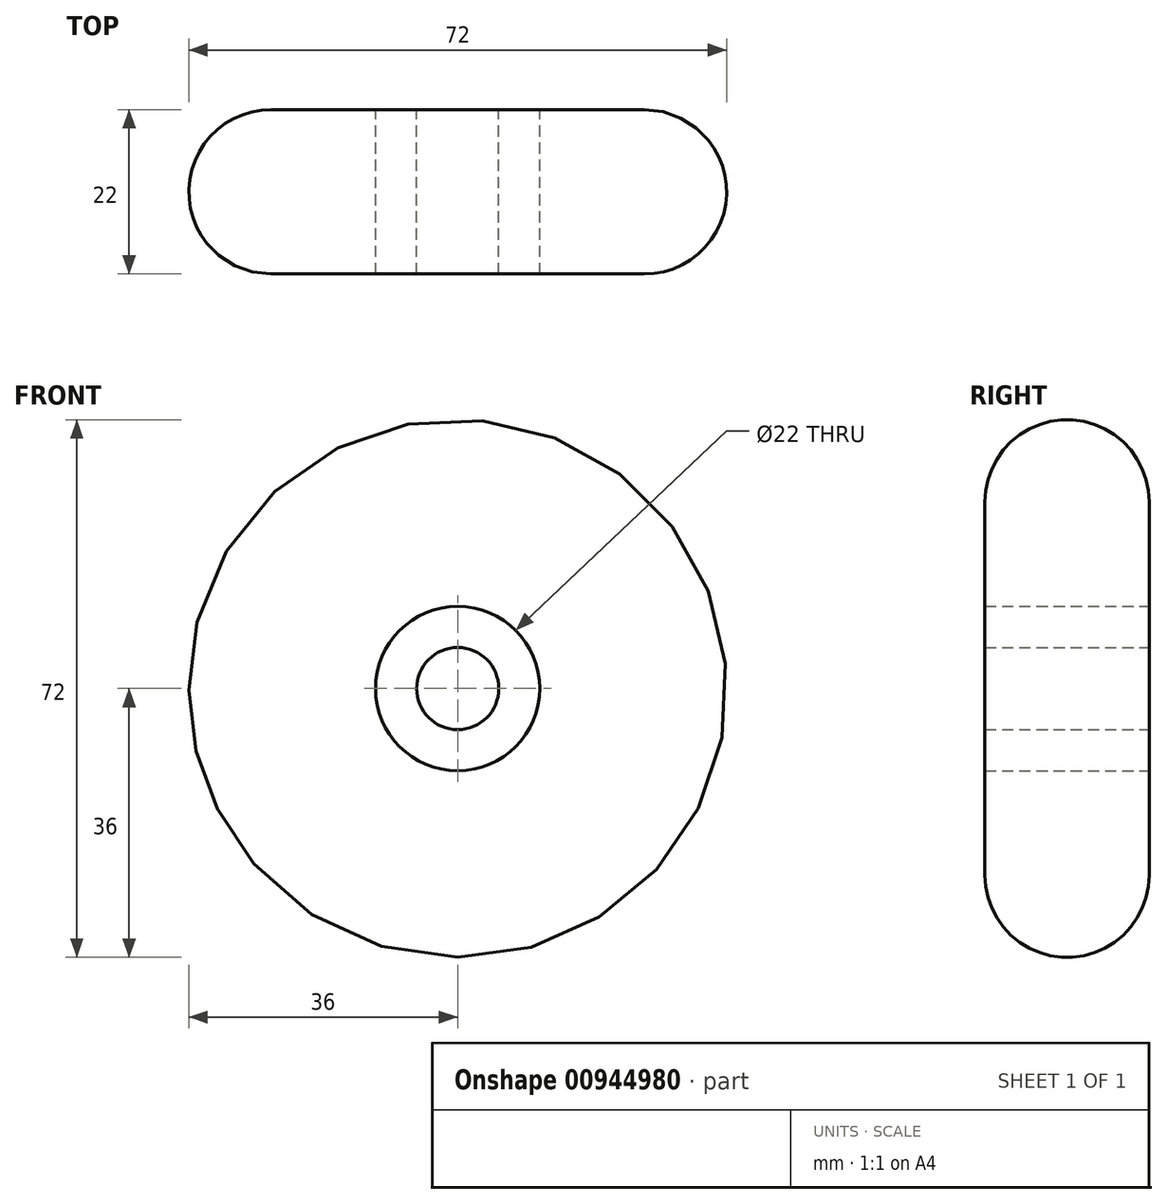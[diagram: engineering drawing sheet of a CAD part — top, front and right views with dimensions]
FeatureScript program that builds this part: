
annotation { "Feature Type Name" : "Feature", "Feature Type Description" : "" }
export const myFeature = defineFeature(function(context is Context, id is Id, definition is map)
    precondition{}
    {
        {
            var Q0;
            Q0=qCreatedBy(makeId("Front.planeOp"),FACE);
            var sketch = newSketch(context, id + "F0", { "sketchPlane" : qUnion([Q0])});
            skCircle(sketch, "E0", {"center": v(0, 0) * mm, "radius": 36 * mm});
            skCircle(sketch, "E1", {"center": v(0, 0) * mm, "radius": 11 * mm});
            skCircle(sketch, "E2", {"center": v(0, 0) * mm, "radius": 5.5 * mm});
            skSolve(sketch);
        }
        {
            var Q0;
            Q0=makeQuery(id+"F0.imprint","IMPRINT",FACE,{"disambiguationData":[TD([[makeQuery(id+"F0.imprint","IMPRINT",EDGE,{"derivedFrom":sQuery(id+"F0.wireOp",EDGE,"E2")}),1.0]])]});
            var Q1;
            Q1=makeQuery(id+"F0.imprint","IMPRINT",FACE,{"disambiguationData":[TD([[makeQuery(id+"F0.imprint","IMPRINT",EDGE,{"derivedFrom":sQuery(id+"F0.wireOp",EDGE,"E0")}),1.0]])]});
            extrude(context, id + "F1", {"entities" : qUnion([Q0, Q1]), "depth" : 22 * mm, "offsetDistance" : 25.4 * mm});
        }
        {
            var Q0;
            Q0=makeQuery(id+"F1.opExtrude","CAP_EDGE",EDGE,{"disambiguationData":[OSD([sQuery(id+"F0.wireOp",EDGE,"E0")])],"isStart":false});
            fillet(context, id + "F2", {"entities" : qUnion([Q0]), "radius" : 11 * mm, "tangentPropagation" : true, "allowEdgeOverflow" : false});
        }
        {
            var Q0;
            Q0=makeQuery(id+"F1.opExtrude","CAP_EDGE",EDGE,{"disambiguationData":[OSD([sQuery(id+"F0.wireOp",EDGE,"E0")])],"isStart":true});
            fillet(context, id + "F3", {"entities" : qUnion([Q0]), "radius" : 11 * mm, "tangentPropagation" : true, "allowEdgeOverflow" : false});
        }
    });
